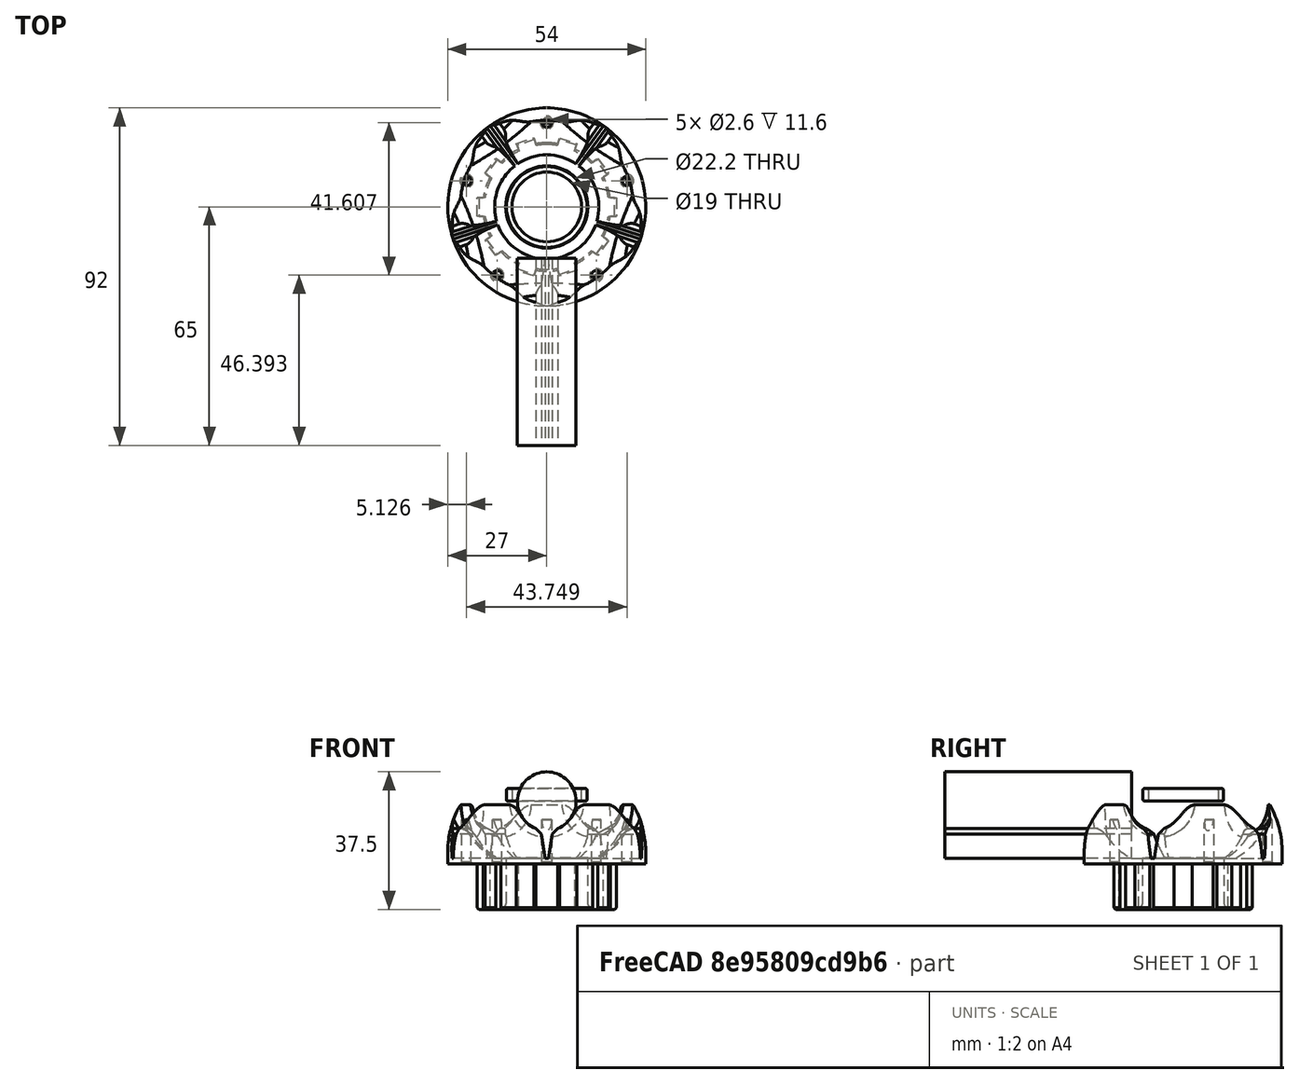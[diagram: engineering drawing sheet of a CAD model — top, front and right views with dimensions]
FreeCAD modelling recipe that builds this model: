
FCSTD DOCUMENT  (FreeCAD 0.20R27770 (Git))
Label: Hinterrad_Flansch
License: All rights reserved
LicenseURL: http://en.wikipedia.org/wiki/All_rights_reserved
objects: Sketcher::SketchObject×7, PartDesign::Body×5, PartDesign::Revolution×3, PartDesign::Pad×3, Part::MultiFuse×2, Part::Fillet×2, PartDesign::PolarPattern×2, Part::FeaturePython×1, PartDesign::Pocket×1, PartDesign::Chamfer×1, Part::Cut×1, PartDesign::Fillet×1
note: 37 computed .brp shape members not serialized (recipe doc carries the construction recipe); baked Part::Feature solids carry a one-line shape summary decoded from their .brp

FEATURE [Sketcher::SketchObject] Sketch
  FullyConstrained = true
  MapMode = 5
  Placement = pos=(0,0,0) rot=(1,0,0;1.5708rad)
  Support = -> [XZ_Plane]
  sketch-geometry (9):
    g0: LineSegment StartX=-66 StartY=5.5 StartZ=0 EndX=-80 EndY=5.5 EndZ=0
    g1: LineSegment StartX=-80 StartY=5.5 StartZ=0 EndX=-80 EndY=15.5 EndZ=0
    g2: LineSegment StartX=-80 StartY=15.5 StartZ=0 EndX=-65 EndY=15.5 EndZ=0
    g3: LineSegment StartX=-65 StartY=-15.5 StartZ=0 EndX=-80 EndY=-15.5 EndZ=0
    g4: LineSegment StartX=-80 StartY=-15.5 StartZ=0 EndX=-80 EndY=-5.5 EndZ=0
    g5: LineSegment StartX=-80 StartY=-5.5 StartZ=0 EndX=-66 EndY=-5.5 EndZ=0
    g6: LineSegment StartX=-66 StartY=-5.5 StartZ=0 EndX=-66 EndY=5.5 EndZ=0
    g7: ArcOfCircle CenterX=-70 CenterY=-6e-16 CenterZ=0 NormalX=0 NormalY=0 NormalZ=1 AngleXU=0 Radius=16.2865 StartAngle=5.02443 EndAngle=7.54194
    g8: GeomPoint X=80 Y=15.5 Z=0
  constraints (24):
    c: Horizontal(g0)
    c: Coincident(g0,g1)
    c: Vertical(g1)
    c: Coincident(g1,g2)
    c: Horizontal(g2)
    c: Horizontal(g3)
    c: Coincident(g3,g4)
    c: Vertical(g4)
    c: Coincident(g4,g5)
    c: Horizontal(g5)
    c: Coincident(g5,g6)
    c: Coincident(g6,g0)
    c: Symmetric(g2,g3,g-1)
    c: Symmetric(g0,g5,g-1)
    c: PointOnObject(g4,g1)
    c: Coincident(g7,g2)
    c: Coincident(g7,g3)
    c: DistanceX(g7,g3) = 5
    c: DistanceY(g3,g1) = 31
    c: DistanceY(g4,g0) = 11
    c: DistanceX(g4,g5) = 14
    c: DistanceX(g2,g2) = 15
    c: Symmetric(g8,g1,g-2)
    c: DistanceX(g1,g8) = 160
FEATURE [PartDesign::Revolution] Revolution
  Angle = 360
  Axis = (0,-2e-16,1)
  Base = (0,0,0)
  Placement = pos=(0,0,0) rot=(1,0,0;1.5708rad)
  Profile = -> Sketch
  ReferenceAxis = -> Sketch [V_Axis]
FEATURE [PartDesign::Body] Body  label="Felge"
  Group = -> [Sketch,Revolution]
  Origin = -> Origin
  Tip = -> Revolution
FEATURE [Sketcher::SketchObject] Sketch002
  ExternalGeometry = -> [Sketch]
  FullyConstrained = true
  MapMode = 5
  Placement = pos=(0,0,0) rot=(1,0,0;1.5708rad)
  Support = -> [XZ_Plane002]
  sketch-geometry (14):
    g0: LineSegment StartX=-11.2 StartY=-15.5 StartZ=0 EndX=-14.2 EndY=-15.5 EndZ=0
    g1: LineSegment StartX=-14.2 StartY=15.5 StartZ=0 EndX=-11.2 EndY=15.5 EndZ=0
    g2: LineSegment StartX=-11.2 StartY=15.5 StartZ=0 EndX=-11.2 EndY=8.5 EndZ=0
    g3: LineSegment StartX=-11.2 StartY=8.5 StartZ=0 EndX=-9.9 EndY=8.5 EndZ=0
    g4: LineSegment StartX=-9.9 StartY=8.5 StartZ=0 EndX=-9.9 EndY=6.5 EndZ=0
    g5: LineSegment StartX=-9.9 StartY=6.5 StartZ=0 EndX=-13.9 EndY=2.5 EndZ=0
    g6: LineSegment StartX=-13.9 StartY=2.5 StartZ=0 EndX=-13.9 EndY=-2.5 EndZ=0
    g7: LineSegment StartX=-13.9 StartY=-2.5 StartZ=0 EndX=-9.9 EndY=-6.5 EndZ=0
    g8: LineSegment StartX=-9.9 StartY=-6.5 StartZ=0 EndX=-9.9 EndY=-8.5 EndZ=0
    g9: LineSegment StartX=-9.9 StartY=-8.5 StartZ=0 EndX=-11.2 EndY=-8.5 EndZ=0
    g10: LineSegment StartX=-11.2 StartY=-8.5 StartZ=0 EndX=-11.2 EndY=-15.5 EndZ=0
    g11: ArcOfCircle CenterX=-6.2 CenterY=2e-16 CenterZ=0 NormalX=0 NormalY=0 NormalZ=1 AngleXU=0 Radius=17.4428 StartAngle=2.04726 EndAngle=4.23592
    g12: GeomPoint X=11.2 Y=-15.5 Z=0
    g13: GeomPoint X=9.9 Y=-8.5 Z=0
  constraints (39):
    c: Horizontal(g0)
    c: Horizontal(g1)
    c: Coincident(g1,g2)
    c: Coincident(g2,g3)
    c: Horizontal(g3)
    c: Coincident(g3,g4)
    c: Vertical(g4)
    c: Coincident(g4,g5)
    c: Coincident(g5,g6)
    c: Coincident(g6,g7)
    c: Coincident(g7,g8)
    c: Vertical(g8)
    c: Coincident(g8,g9)
    c: Horizontal(g9)
    c: Coincident(g9,g10)
    c: Coincident(g10,g0)
    c: Coincident(g11,g1)
    c: Coincident(g11,g0)
    c: Vertical(g2)
    c: Vertical(g10)
    c: Equal(g10,g2)
    c: Equal(g3,g9)
    c: Equal(g8,g4)
    c: Equal(g1,g0)
    c: Symmetric(g0,g1,g-1)
    c: Symmetric(g6,g5,g-1)
    c: Angle(g7) = -0.785398
    c: DistanceX(g0,g11) = 8
    c: DistanceY(g10,g10) = 7
    c: Symmetric(g8,g13,g-2)
    c: Symmetric(g12,g0,g-2)
    c: DistanceX(g0,g12) = 22.4
    c: DistanceX(g8,g13) = 19.8
    c: DistanceX(g9,g9) = 1.3
    c: DistanceY(g4,g4) = 2
    c: DistanceY(g6,g6) = 5
    c: DistanceX(g1,g1) = 3
    c: PointOnObject(g-3,g0)
    c: DistanceX(g1) = -11.2
FEATURE [PartDesign::Revolution] Revolution001
  Angle = 360
  Axis = (0,-2e-16,1)
  Base = (0,0,0)
  Placement = pos=(0,0,0) rot=(1,0,0;1.5708rad)
  Profile = -> Sketch002
  ReferenceAxis = -> Sketch002 [V_Axis]
FEATURE [PartDesign::Body] Body001  label="Nabe"
  Group = -> [Revolution001]
  Origin = -> Origin001
  Tip = -> Revolution001
FEATURE [Sketcher::SketchObject] Sketch003
  AttachmentOffset = pos=(0,0,14) rot=(0,0,1;0rad)
  FullyConstrained = true
  MapMode = 5
  Placement = pos=(0,-14,-3.1e-15) rot=(1,0,0;1.5708rad)
  Support = -> [XZ_Plane003]
  sketch-geometry (6):
    g0: ArcOfCircle CenterX=0 CenterY=0 CenterZ=0 NormalX=0 NormalY=0 NormalZ=1 AngleXU=0 Radius=8 StartAngle=5.09679 EndAngle=10.6112
    g1: LineSegment StartX=1.5 StartY=-8.9162 StartZ=0 EndX=0.5 EndY=-15.5 EndZ=0
    g2: LineSegment StartX=0.5 StartY=-15.5 StartZ=0 EndX=-0.5 EndY=-15.5 EndZ=0
    g3: LineSegment StartX=-0.5 StartY=-15.5 StartZ=0 EndX=-1.5 EndY=-8.9162 EndZ=0
    g4: LineSegment StartX=-3 StartY=-7.4162 StartZ=0 EndX=-1.5 EndY=-8.9162 EndZ=0
    g5: LineSegment StartX=1.5 StartY=-8.9162 StartZ=0 EndX=3 EndY=-7.4162 EndZ=0
  constraints (16):
    c: Coincident(g0,g-1)
    c: Coincident(g1,g2)
    c: Coincident(g2,g3)
    c: Symmetric(g0,g0,g-2)
    c: Symmetric(g2,g1,g-2)
    c: DistanceY(g1) = -15.5
    c: DistanceX(g2,g2) = 1
    c: Diameter(g0) = 16
    c: Symmetric(g1,g3,g-2)
    c: DistanceX(g3,g1) = 3
    c: Coincident(g4,g0)
    c: Coincident(g4,g3)
    c: Coincident(g5,g1)
    c: Coincident(g5,g0)
    c: DistanceX(g0,g0) = 6
    c: Angle(g5) = 0.785398
FEATURE [PartDesign::Pad] Pad
  Direction = (0,-1,-2e-16)
  Length = 51
  Length2 = 100
  Placement = pos=(0,0,0) rot=(1,0,0;1.5708rad)
  Profile = -> Sketch003
  Type = 0
FEATURE [PartDesign::Body] Body002  label="Speiche"
  Group = -> [Sketch003,Pad]
  Origin = -> Origin002
  Tip = -> Pad
FEATURE [Part::FeaturePython] Array  label="Speichen"  # Draft array (typed FeaturePython)
  AlwaysSyncPlacement = false
  Angle = 360
  ArrayType = 1
  Axis = (0,0,1)
  Base = -> Body002
  Center = (0,0,0)
  Count = 5
  ExpandArray = false
  Fuse = false
  IntervalAxis = (0,0,0)
  IntervalX = (50,0,0)
  IntervalY = (0,50,0)
  IntervalZ = (0,0,50)
  NumberCircles = 3
  NumberPolar = 5
  NumberX = 2
  NumberY = 2
  NumberZ = 1
  PlacementList = 5 placements: [(0,0,0),(0,0,0),(0,0,0),(0,0,0),(0,0,0)]
  RadialDistance = 50
  ScaleList = (5) [(1,1,1),(1,1,1),(1,1,1),(1,1,1),(1,1,1)]
  Symmetry = 1
  TangentialDistance = 25
FEATURE [Part::MultiFuse] Fusion
  Shapes = -> [Body,Array]
FEATURE [Part::Fillet] Fillet
  Base = -> Fusion
  Edges = 9 edges: [Edge1 r=1,Edge28 r=1,Edge35 r=3,Edge41 r=3,Edge47 r=3,Edge53 r=3,Edge59 r=3,Edge73 r=1,Edge136 r=1]
FEATURE [Part::MultiFuse] Fusion001
  Shapes = -> [Fillet,Body001]
FEATURE [Part::Fillet] Fillet001  label="160mm"
  Base = -> Fusion001
  Edges = 5 edges r=4: [Edge4,Edge11,Edge20,Edge28,Edge36]
FEATURE [Sketcher::SketchObject] Sketch004  label="Profil"
  FullyConstrained = true
  MapMode = 5
  Placement = pos=(0,0,0) rot=(0.57735,0.57735,0.57735;2.0944rad)
  Support = -> [YZ_Plane003]
  sketch-geometry (14):
    g0: LineSegment StartX=11.1 StartY=-15.5 StartZ=0 EndX=11.1 EndY=-27.5 EndZ=0
    g1: LineSegment StartX=13.1 StartY=-29.5 StartZ=0 EndX=17 EndY=-29.5 EndZ=0
    g2: LineSegment StartX=17.5 StartY=-29 StartZ=0 EndX=17.5 EndY=-17.1 EndZ=0
    g3: LineSegment StartX=17.5 StartY=-17.1 StartZ=0 EndX=27 EndY=-17.1 EndZ=0
    g4: LineSegment StartX=27 StartY=-17.1 StartZ=0 EndX=27 EndY=-14.1 EndZ=0
    g5: LineSegment StartX=23.0259 StartY=0 StartZ=0 EndX=11.1 EndY=-15.5 EndZ=0
    g6: GeomPoint X=-11.1 Y=-15.5 Z=0
    g7: GeomPoint X=-17.5 Y=-29.5 Z=0
    g8: GeomPoint X=-27 Y=-14.1 Z=0
    g9: ArcOfCircle CenterX=0 CenterY=-14.1 CenterZ=0 NormalX=0 NormalY=0 NormalZ=1 AngleXU=0 Radius=27 StartAngle=0 EndAngle=0.549455
    g10: ArcOfCircle CenterX=13.1 CenterY=-27.5 CenterZ=0 NormalX=0 NormalY=0 NormalZ=1 AngleXU=0 Radius=2 StartAngle=3.14159 EndAngle=4.71239
    g11: GeomPoint X=11.1 Y=-29.5 Z=0
    g12: GeomPoint X=17.5 Y=-29.5 Z=0
    g13: LineSegment StartX=17 StartY=-29.5 StartZ=0 EndX=17.5 EndY=-29 EndZ=0
  constraints (33):
    c: Vertical(g0)
    c: Horizontal(g1)
    c: Vertical(g2)
    c: Coincident(g2,g3)
    c: Horizontal(g3)
    c: Coincident(g3,g4)
    c: Vertical(g4)
    c: Coincident(g5,g0)
    c: Symmetric(g0,g6,g-2)
    c: Symmetric(g12,g7,g-2)
    c: Symmetric(g8,g4,g-2)
    c: DistanceX(g8,g4) = 54
    c: DistanceX(g7,g12) = 35
    c: DistanceX(g6,g0) = 22.2
    c: DistanceY(g6) = -15.5
    c: Coincident(g5,g9)
    c: DistanceY(g11,g0) = 14
    c: DistanceY(g12,g2) = 12.4
    c: PointOnObject(g9,g-2)
    c: Tangent(g9,g4) = -1.5708
    c: PointOnObject(g5,g-1)
    c: DistanceY(g4,g4) = 3
    c: PointOnObject(g11,g0)
    c: PointOnObject(g11,g1)
    c: Tangent(g0,g10) = -1.5708
    c: Tangent(g1,g10) = -1.5708
    c: Radius(g10) = 2
    c: PointOnObject(g12,g2)
    c: Coincident(g13,g1)
    c: Coincident(g13,g2)
    c: Angle(g13) = 0.785398
    c: DistanceX(g1,g12) = 0.5
    c: PointOnObject(g12,g1)
FEATURE [PartDesign::Revolution] Revolution002
  Angle = 360
  Axis = (-2e-16,3e-16,1)
  Base = (0,0,0)
  Placement = pos=(0,0,0) rot=(0.57735,0.57735,0.57735;2.0944rad)
  Profile = -> Sketch004
  ReferenceAxis = -> Sketch004 [V_Axis]
  Reversed = true
FEATURE [Sketcher::SketchObject] Sketch005  label="Schraubenloch"
  AttachmentOffset = pos=(0,0,-5) rot=(0,0,1;0rad)
  FullyConstrained = true
  MapMode = 5
  Placement = pos=(0,0,-5) rot=(0,0,1;0rad)
  Support = -> [XY_Plane003]
  sketch-geometry (1):
    g0: Circle CenterX=0 CenterY=23 CenterZ=0 NormalX=0 NormalY=0 NormalZ=1 AngleXU=0 Radius=1.3
  constraints (3):
    c: PointOnObject(g0,g-2)
    c: Diameter(g0) = 2.6
    c: DistanceY(g0) = 23
FEATURE [PartDesign::Pocket] Pocket
  BaseFeature = -> Revolution002
  Direction = (0,0,-1)
  Length = 5
  Length2 = 5
  Placement = pos=(0,0,0) rot=(0.57735,0.57735,0.57735;2.0944rad)
  Profile = -> Sketch005
  ReferenceAxis = -> Sketch005 [N_Axis]
  Type = 1
FEATURE [PartDesign::PolarPattern] PolarPattern
  Angle = 360
  Axis = -> Sketch005 [N_Axis]
  BaseFeature = -> Pocket
  Occurrences = 5
  Originals = -> [Pocket]
  Overlap = 0
  Placement = pos=(0,0,0) rot=(0.57735,0.57735,0.57735;2.0944rad)
FEATURE [Sketcher::SketchObject] Sketch006
  FullyConstrained = true
  MapMode = 5
  Placement = pos=(2.62e-14,-1.47e-14,-29.5) rot=(0.707107,0.707107,0;3.14159rad)
  Support = -> [PolarPattern]
  sketch-geometry (4):
    g0: LineSegment StartX=-2.5 StartY=19 StartZ=0 EndX=2.5 EndY=19 EndZ=0
    g1: LineSegment StartX=2.5 StartY=19 StartZ=0 EndX=2.5 EndY=14 EndZ=0
    g2: LineSegment StartX=2.5 StartY=14 StartZ=0 EndX=-2.5 EndY=14 EndZ=0
    g3: LineSegment StartX=-2.5 StartY=14 StartZ=0 EndX=-2.5 EndY=19 EndZ=0
  constraints (11):
    c: Coincident(g0,g1)
    c: Coincident(g1,g2)
    c: Coincident(g2,g3)
    c: Coincident(g3,g0)
    c: Horizontal(g0)
    c: Vertical(g1)
    c: Vertical(g3)
    c: Symmetric(g1,g2,g-2)
    c: DistanceX(g2,g2) = 5
    c: Equal(g3,g0)
    c: DistanceY(g0) = 19
FEATURE [PartDesign::Pad] Pad001
  BaseFeature = -> PolarPattern
  Direction = (9e-16,-5e-16,-1)
  Length = 13
  Length2 = 10
  Placement = pos=(0,0,0) rot=(0.57735,0.57735,0.57735;2.0944rad)
  Profile = -> Sketch006
  ReferenceAxis = -> Sketch006 [N_Axis]
  Reversed = true
  Type = 0
FEATURE [PartDesign::PolarPattern] PolarPattern001
  Angle = 360
  Axis = -> Sketch006 [N_Axis]
  BaseFeature = -> Pad001
  Occurrences = 10
  Originals = -> [Pad001]
  Overlap = 0
  Placement = pos=(0,0,0) rot=(0.57735,0.57735,0.57735;2.0944rad)
FEATURE [PartDesign::Chamfer] Chamfer
  Angle = 45
  Base = -> PolarPattern001 [Edge160,Edge167,Edge174,Edge140,Edge98,Edge181,Edge97,Edge188,Edge195,Edge95,Edge202,Edge209,Edge96,Edge146,Edge153]
  BaseFeature = -> PolarPattern001
  ChamferType = 0
  FlipDirection = false
  Placement = pos=(0,0,0) rot=(0.57735,0.57735,0.57735;2.0944rad)
  Size = 0.5
  Size2 = 1
  SupportTransform = false
  UseAllEdges = false
FEATURE [PartDesign::Body] Body003  label="Flansch"
  Group = -> [Sketch004,Revolution002,Sketch005,Pocket,PolarPattern,Sketch006,Pad001,PolarPattern001,Chamfer]
  Origin = -> Origin003
  Tip = -> Chamfer
FEATURE [Part::Cut] Cut  label="Krone"
  Base = -> Body003
  Tool = -> Fillet001
FEATURE [Sketcher::SketchObject] Sketch007
  FullyConstrained = true
  MapMode = 5
  Support = -> [XY_Plane004]
  sketch-geometry (2):
    g0: Circle CenterX=0 CenterY=0 CenterZ=0 NormalX=0 NormalY=0 NormalZ=1 AngleXU=0 Radius=9.5
    g1: Circle CenterX=0 CenterY=0 CenterZ=0 NormalX=0 NormalY=0 NormalZ=1 AngleXU=0 Radius=11
  constraints (4):
    c: Coincident(g0,g-1)
    c: Coincident(g1,g0)
    c: Diameter(g1) = 22
    c: Diameter(g0) = 19
FEATURE [PartDesign::Pad] Pad002
  Direction = (0,0,1)
  Length = 3.5
  Length2 = 10
  Profile = -> Sketch007
  ReferenceAxis = -> Sketch007 [N_Axis]
  Type = 0
FEATURE [PartDesign::Fillet] Fillet002
  Base = -> Pad002 [Face3,Face4]
  BaseFeature = -> Pad002
  Radius = 0.5
  SupportTransform = false
  UseAllEdges = false
FEATURE [PartDesign::Body] Body004  label="Ring22mm"
  Group = -> [Sketch007,Pad002,Fillet002]
  Origin = -> Origin004
  Tip = -> Fillet002
